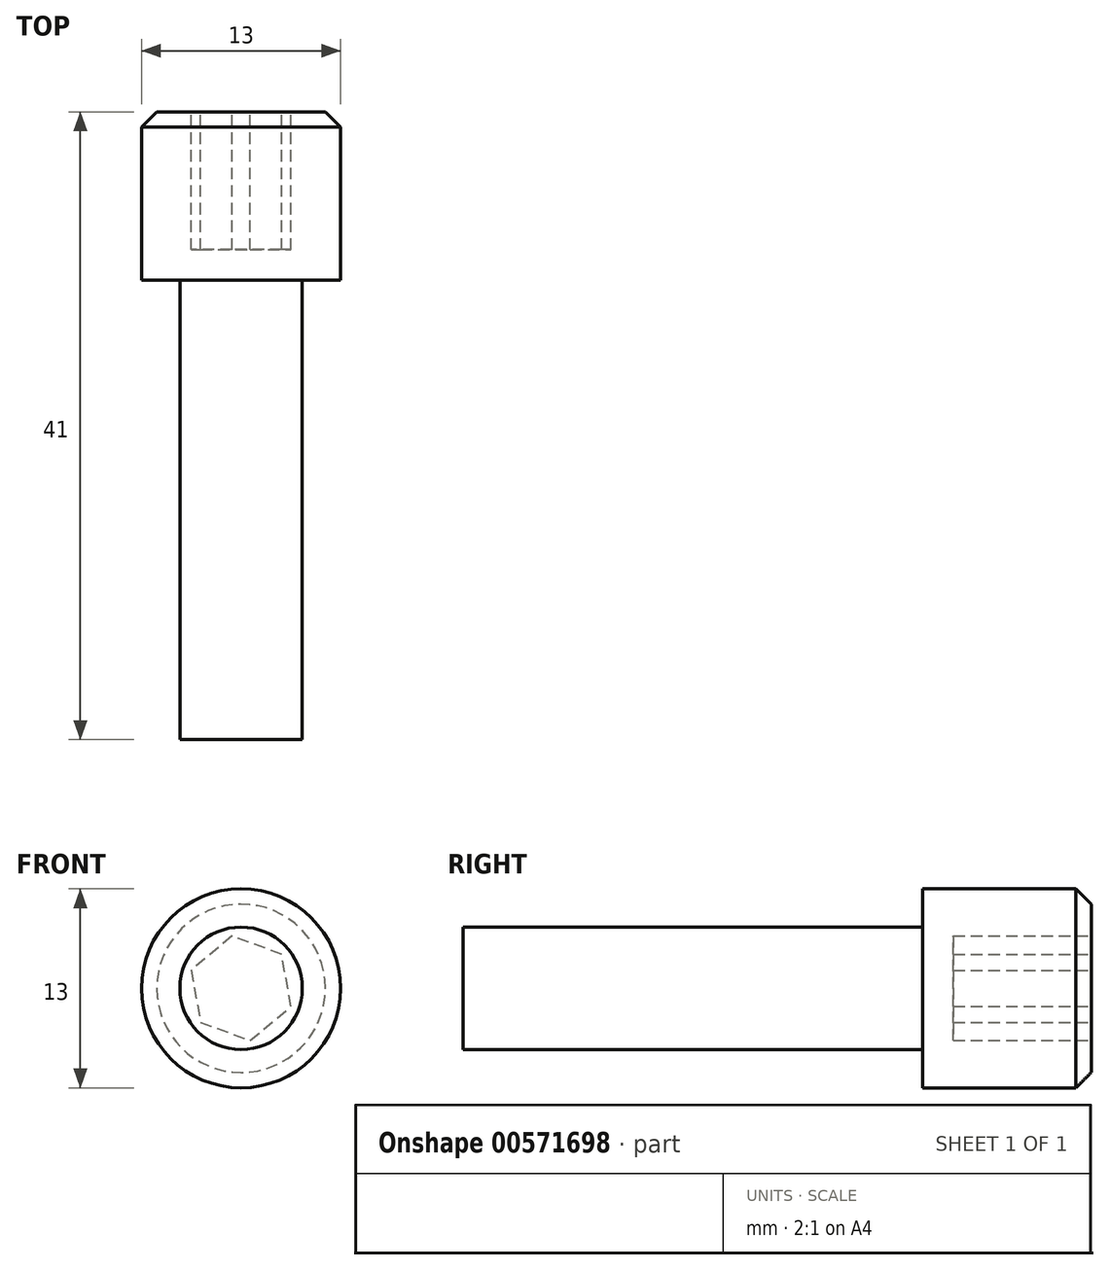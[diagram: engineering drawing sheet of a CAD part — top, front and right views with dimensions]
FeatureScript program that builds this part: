
annotation { "Feature Type Name" : "Feature", "Feature Type Description" : "" }
export const myFeature = defineFeature(function(context is Context, id is Id, definition is map)
    precondition{}
    {
        {
            var Q0;
            Q0=qCreatedBy(makeId("Top.planeOp"),FACE);
            var sketch = newSketch(context, id + "F0", { "sketchPlane" : qUnion([Q0])});
            skLineSegment(sketch, "E0", {"start": v(0, 0) * mm, "end": v(0, 41) * mm});
            skLineSegment(sketch, "E1", {"start": v(0, 41) * mm, "end": v(-6.5, 41) * mm});
            skLineSegment(sketch, "E2", {"start": v(-6.5, 41) * mm, "end": v(-6.5, 30) * mm});
            skLineSegment(sketch, "E3", {"start": v(-6.5, 30) * mm, "end": v(-4, 30) * mm});
            skLineSegment(sketch, "E4", {"start": v(-4, 30) * mm, "end": v(-4, 0) * mm});
            skLineSegment(sketch, "E5", {"start": v(-4, 0) * mm, "end": v(0, 0) * mm});
            skSolve(sketch);
        }
        {
            var Q0;
            Q0=makeQuery(id+"F0.imprint","IMPRINT",FACE,{"disambiguationData":[TD([[makeQuery(id+"F0.imprint","IMPRINT",EDGE,{"derivedFrom":sQuery(id+"F0.wireOp",EDGE,"E0")}),1.0]])]});
            var Q1;
            Q1=sQuery(id+"F0.wireOp",EDGE,"E0");
            revolve(context, id + "F1", {"entities" : qUnion([Q0]), "axis" : qUnion([Q1]), "revolveType" : RevolveType.FULL});
        }
        {
            var Q0;
            Q0=makeQuery(id+"F1.opRevolve","SWEPT_FACE",FACE,{"disambiguationData":[OSD([sQuery(id+"F0.wireOp",EDGE,"E1")])]});
            var sketch = newSketch(context, id + "F2", { "sketchPlane" : qUnion([Q0])});
            skCircle(sketch, "E6.cCircle", {"center": v(0, 0) * mm, "radius": 3 * mm, "construction": true});
            skLineSegment(sketch, "E6.0", {"start": v(-0.6, -3.41) * mm, "end": v(-3.26, -1.18) * mm});
            skLineSegment(sketch, "E6.1", {"start": v(-3.26, -1.18) * mm, "end": v(-2.65, 2.23) * mm});
            skLineSegment(sketch, "E6.2", {"start": v(-2.65, 2.23) * mm, "end": v(0.6, 3.41) * mm});
            skLineSegment(sketch, "E6.3", {"start": v(0.6, 3.41) * mm, "end": v(3.26, 1.18) * mm});
            skLineSegment(sketch, "E6.4", {"start": v(3.26, 1.18) * mm, "end": v(2.65, -2.23) * mm});
            skLineSegment(sketch, "E6.5", {"start": v(2.65, -2.23) * mm, "end": v(-0.6, -3.41) * mm});
            skPoint(sketch, "E6.0.midPoint", {"position": v(-1.93, -2.3) * mm});
            skSolve(sketch);
        }
        {
            var Q0;
            Q0 = qSketchRegion(id + "F2", true);
            extrude(context, id + "F3", {"entities" : qUnion([Q0]), "operationType" : NewBodyOperationType.REMOVE, "oppositeDirection" : true, "depth" : 9 * mm, "offsetDistance" : 25 * mm});
        }
        {
            var Q0;
            Q0=makeQuery(id+"F1.opRevolve","SWEPT_EDGE",EDGE,{"disambiguationData":[OSD([sQuery(id+"F0.wireOp",EDGE,"E1"),sQuery(id+"F0.wireOp",EDGE,"E2")])]});
            chamfer(context, id + "F4", {"entities" : qUnion([Q0]), "width" : 1 * mm, "tangentPropagation" : true});
        }
    });
